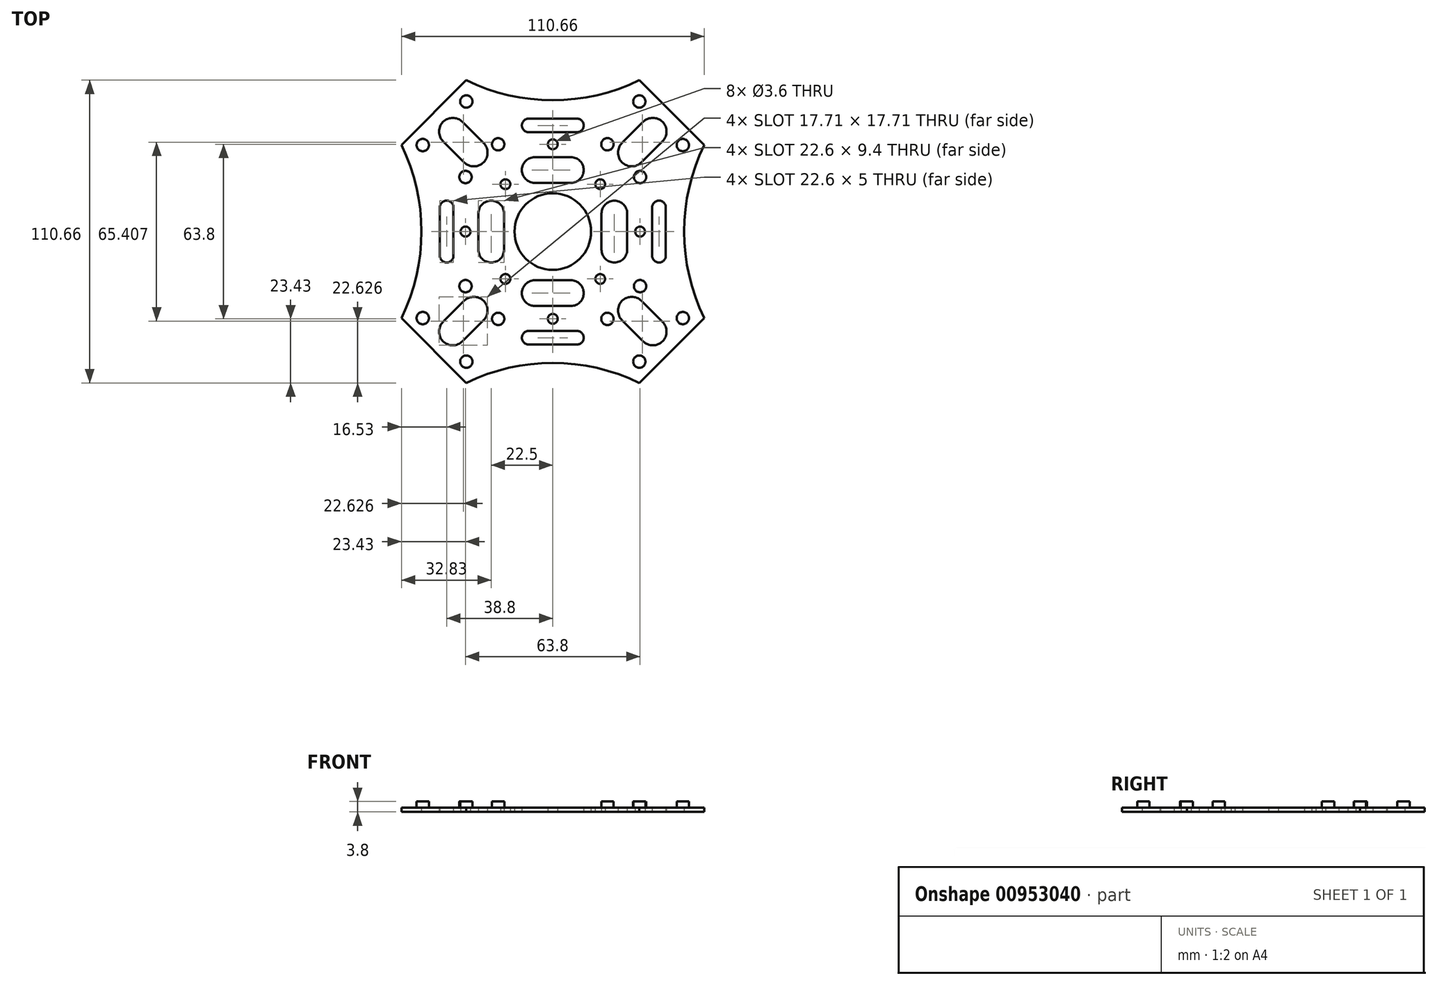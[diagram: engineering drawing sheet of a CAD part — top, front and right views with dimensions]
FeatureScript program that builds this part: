
annotation { "Feature Type Name" : "Feature", "Feature Type Description" : "" }
export const myFeature = defineFeature(function(context is Context, id is Id, definition is map)
    precondition{}
    {
        {
            var Q0;
            Q0=qCreatedBy(makeId("Top.planeOp"),FACE);
            var sketch = newSketch(context, id + "F0", { "sketchPlane" : qUnion([Q0])});
            skCircle(sketch, "E0", {"center": v(0, 0) * mm, "radius": 14 * mm});
            skLineSegment(sketch, "E1", {"start": v(0, 0) * mm, "end": v(83.05, 0) * mm, "construction": true});
            skLineSegment(sketch, "E2", {"start": v(0, 0) * mm, "end": v(67.55, 67.55) * mm, "construction": true});
            skLineSegment(sketch, "E3", {"start": v(17.8, 0) * mm, "end": v(17.8, 6.6) * mm});
            skLineSegment(sketch, "E4", {"start": v(27.2, 0) * mm, "end": v(27.2, 6.6) * mm});
            skArc(sketch, "E5", {"start": v(27.2, 6.6) * mm, "mid": v(22.5, 11.3) * mm, "end": v(17.8, 6.6) * mm});
            skLineSegment(sketch, "E6", {"start": v(36.3, 0) * mm, "end": v(36.3, 8.8) * mm});
            skLineSegment(sketch, "E7", {"start": v(41.3, 0) * mm, "end": v(41.3, 8.8) * mm});
            skArc(sketch, "E8", {"start": v(41.3, 8.8) * mm, "mid": v(38.8, 11.3) * mm, "end": v(36.3, 8.8) * mm});
            skArc(sketch, "E9", {"start": v(33.7, 0) * mm, "mid": v(31.9, 1.8) * mm, "end": v(30.1, 0) * mm});
            skLineSegment(sketch, "E10", {"start": v(32.39, 25.31) * mm, "end": v(40.1, 33.02) * mm});
            skArc(sketch, "E11", {"start": v(32.39, 25.31) * mm, "mid": v(28.85, 23.85) * mm, "end": v(25.31, 25.31) * mm});
            skArc(sketch, "E12", {"start": v(40.1, 33.02) * mm, "mid": v(41.56, 36.56) * mm, "end": v(40.1, 40.1) * mm});
            skLineSegment(sketch, "E13", {"start": v(43.49, 43.49) * mm, "end": v(55.33, 31.64) * mm});
            skArc(sketch, "E14", {"start": v(55.33, 31.64) * mm, "mid": v(49.86, 16.24) * mm, "end": v(48, 0) * mm});
            skArc(sketch, "E15", {"start": v(16.05, 16.05) * mm, "mid": v(18.6, 16.05) * mm, "end": v(18.6, 18.6) * mm});
            skLineSegment(sketch, "E16.MirrorCS", {"start": v(43.49, 43.49) * mm, "end": v(31.64, 55.33) * mm});
            skArc(sketch, "E17.MirrorCS", {"start": v(31.64, 55.33) * mm, "mid": v(16.24, 49.86) * mm, "end": v(0, 48) * mm});
            skArc(sketch, "E18.MirrorCS", {"start": v(33.02, 40.1) * mm, "mid": v(36.56, 41.56) * mm, "end": v(40.1, 40.1) * mm});
            skLineSegment(sketch, "E19.MirrorCS", {"start": v(25.31, 32.39) * mm, "end": v(33.02, 40.1) * mm});
            skArc(sketch, "E20.MirrorCS", {"start": v(25.31, 32.39) * mm, "mid": v(23.85, 28.85) * mm, "end": v(25.31, 25.31) * mm});
            skArc(sketch, "E21.MirrorCS", {"start": v(6.6, 27.2) * mm, "mid": v(11.3, 22.5) * mm, "end": v(6.6, 17.8) * mm});
            skLineSegment(sketch, "E22.MirrorCS", {"start": v(0, 17.8) * mm, "end": v(6.6, 17.8) * mm});
            skLineSegment(sketch, "E23.MirrorCS", {"start": v(0, 27.2) * mm, "end": v(6.6, 27.2) * mm});
            skLineSegment(sketch, "E24.MirrorCS", {"start": v(0, 36.3) * mm, "end": v(8.8, 36.3) * mm});
            skArc(sketch, "E25.MirrorCS", {"start": v(8.8, 41.3) * mm, "mid": v(11.3, 38.8) * mm, "end": v(8.8, 36.3) * mm});
            skLineSegment(sketch, "E26.MirrorCS", {"start": v(0, 41.3) * mm, "end": v(8.8, 41.3) * mm});
            skArc(sketch, "E27.MirrorCS", {"start": v(55.33, -31.64) * mm, "mid": v(49.86, -16.24) * mm, "end": v(48, 0) * mm});
            skLineSegment(sketch, "E28.MirrorCS", {"start": v(41.3, 0) * mm, "end": v(41.3, -8.8) * mm});
            skLineSegment(sketch, "E29.MirrorCS", {"start": v(36.3, 0) * mm, "end": v(36.3, -8.8) * mm});
            skLineSegment(sketch, "E30.MirrorCS", {"start": v(27.2, 0) * mm, "end": v(27.2, -6.6) * mm});
            skLineSegment(sketch, "E31.MirrorCS", {"start": v(17.8, 0) * mm, "end": v(17.8, -6.6) * mm});
            skArc(sketch, "E32.MirrorCS", {"start": v(27.2, -6.6) * mm, "mid": v(22.5, -11.3) * mm, "end": v(17.8, -6.6) * mm});
            skArc(sketch, "E33.MirrorCS", {"start": v(41.3, -8.8) * mm, "mid": v(38.8, -11.3) * mm, "end": v(36.3, -8.8) * mm});
            skLineSegment(sketch, "E34.MirrorCS", {"start": v(32.39, -25.31) * mm, "end": v(40.1, -33.02) * mm});
            skArc(sketch, "E35.MirrorCS", {"start": v(32.39, -25.31) * mm, "mid": v(28.85, -23.85) * mm, "end": v(25.31, -25.31) * mm});
            skArc(sketch, "E36.MirrorCS", {"start": v(25.31, -32.39) * mm, "mid": v(23.85, -28.85) * mm, "end": v(25.31, -25.31) * mm});
            skLineSegment(sketch, "E37.MirrorCS", {"start": v(25.31, -32.39) * mm, "end": v(33.02, -40.1) * mm});
            skArc(sketch, "E38.MirrorCS", {"start": v(33.02, -40.1) * mm, "mid": v(36.56, -41.56) * mm, "end": v(40.1, -40.1) * mm});
            skArc(sketch, "E39.MirrorCS", {"start": v(40.1, -33.02) * mm, "mid": v(41.56, -36.56) * mm, "end": v(40.1, -40.1) * mm});
            skLineSegment(sketch, "E40.MirrorCS", {"start": v(43.49, -43.49) * mm, "end": v(55.33, -31.64) * mm});
            skLineSegment(sketch, "E41.MirrorCS", {"start": v(43.49, -43.49) * mm, "end": v(31.64, -55.33) * mm});
            skArc(sketch, "E42.MirrorCS", {"start": v(31.64, -55.33) * mm, "mid": v(16.24, -49.86) * mm, "end": v(0, -48) * mm});
            skLineSegment(sketch, "E43.MirrorCS", {"start": v(0, -41.3) * mm, "end": v(8.8, -41.3) * mm});
            skArc(sketch, "E44.MirrorCS", {"start": v(8.8, -41.3) * mm, "mid": v(11.3, -38.8) * mm, "end": v(8.8, -36.3) * mm});
            skLineSegment(sketch, "E45.MirrorCS", {"start": v(0, -36.3) * mm, "end": v(8.8, -36.3) * mm});
            skLineSegment(sketch, "E46.MirrorCS", {"start": v(0, -27.2) * mm, "end": v(6.6, -27.2) * mm});
            skArc(sketch, "E47.MirrorCS", {"start": v(6.6, -27.2) * mm, "mid": v(11.3, -22.5) * mm, "end": v(6.6, -17.8) * mm});
            skLineSegment(sketch, "E48.MirrorCS", {"start": v(0, -17.8) * mm, "end": v(6.6, -17.8) * mm});
            skArc(sketch, "E49.MirrorCS", {"start": v(16.05, 16.05) * mm, "mid": v(16.05, 18.6) * mm, "end": v(18.6, 18.6) * mm});
            skArc(sketch, "E50.MirrorCS", {"start": v(33.7, 0) * mm, "mid": v(31.9, -1.8) * mm, "end": v(30.1, 0) * mm});
            skArc(sketch, "E51.MirrorCS", {"start": v(16.05, -16.05) * mm, "mid": v(18.6, -16.05) * mm, "end": v(18.6, -18.6) * mm});
            skArc(sketch, "E52.MirrorCS", {"start": v(16.05, -16.05) * mm, "mid": v(16.05, -18.6) * mm, "end": v(18.6, -18.6) * mm});
            skArc(sketch, "E53.MirrorCS", {"start": v(0, 33.7) * mm, "mid": v(1.8, 31.9) * mm, "end": v(0, 30.1) * mm});
            skArc(sketch, "E54.MirrorCS", {"start": v(0, -33.7) * mm, "mid": v(1.8, -31.9) * mm, "end": v(0, -30.1) * mm});
            skArc(sketch, "E55.MirrorCS", {"start": v(-33.7, 0) * mm, "mid": v(-31.9, -1.8) * mm, "end": v(-30.1, 0) * mm});
            skArc(sketch, "E56.MirrorCS", {"start": v(-33.7, 0) * mm, "mid": v(-31.9, 1.8) * mm, "end": v(-30.1, 0) * mm});
            skArc(sketch, "E57.MirrorCS", {"start": v(-16.05, 16.05) * mm, "mid": v(-18.6, 16.05) * mm, "end": v(-18.6, 18.6) * mm});
            skArc(sketch, "E58.MirrorCS", {"start": v(-16.05, -16.05) * mm, "mid": v(-18.6, -16.05) * mm, "end": v(-18.6, -18.6) * mm});
            skArc(sketch, "E59.MirrorCS", {"start": v(0, -33.7) * mm, "mid": v(-1.8, -31.9) * mm, "end": v(0, -30.1) * mm});
            skArc(sketch, "E60.MirrorCS", {"start": v(-16.05, 16.05) * mm, "mid": v(-16.05, 18.6) * mm, "end": v(-18.6, 18.6) * mm});
            skArc(sketch, "E61.MirrorCS", {"start": v(-16.05, -16.05) * mm, "mid": v(-16.05, -18.6) * mm, "end": v(-18.6, -18.6) * mm});
            skLineSegment(sketch, "E62.MirrorCS", {"start": v(0, 41.3) * mm, "end": v(-8.8, 41.3) * mm});
            skLineSegment(sketch, "E63.MirrorCS", {"start": v(-36.3, 0) * mm, "end": v(-36.3, -8.8) * mm});
            skArc(sketch, "E64.MirrorCS", {"start": v(-41.3, -8.8) * mm, "mid": v(-38.8, -11.3) * mm, "end": v(-36.3, -8.8) * mm});
            skArc(sketch, "E65.MirrorCS", {"start": v(-27.2, -6.6) * mm, "mid": v(-22.5, -11.3) * mm, "end": v(-17.8, -6.6) * mm});
            skLineSegment(sketch, "E66.MirrorCS", {"start": v(0, -27.2) * mm, "end": v(-6.6, -27.2) * mm});
            skLineSegment(sketch, "E67.MirrorCS", {"start": v(-36.3, 0) * mm, "end": v(-36.3, 8.8) * mm});
            skLineSegment(sketch, "E68.MirrorCS", {"start": v(-25.31, 32.39) * mm, "end": v(-33.02, 40.1) * mm});
            skLineSegment(sketch, "E69.MirrorCS", {"start": v(0, 36.3) * mm, "end": v(-8.8, 36.3) * mm});
            skLineSegment(sketch, "E70.MirrorCS", {"start": v(0, 17.8) * mm, "end": v(-6.6, 17.8) * mm});
            skLineSegment(sketch, "E71.MirrorCS", {"start": v(-27.2, 0) * mm, "end": v(-27.2, 6.6) * mm});
            skArc(sketch, "E72.MirrorCS", {"start": v(-8.8, 41.3) * mm, "mid": v(-11.3, 38.8) * mm, "end": v(-8.8, 36.3) * mm});
            skArc(sketch, "E73.MirrorCS", {"start": v(0, 33.7) * mm, "mid": v(-1.8, 31.9) * mm, "end": v(0, 30.1) * mm});
            skLineSegment(sketch, "E74.MirrorCS", {"start": v(-27.2, 0) * mm, "end": v(-27.2, -6.6) * mm});
            skArc(sketch, "E75.MirrorCS", {"start": v(-6.6, 27.2) * mm, "mid": v(-11.3, 22.5) * mm, "end": v(-6.6, 17.8) * mm});
            skLineSegment(sketch, "E76.MirrorCS", {"start": v(0, -36.3) * mm, "end": v(-8.8, -36.3) * mm});
            skArc(sketch, "E77.MirrorCS", {"start": v(-27.2, 6.6) * mm, "mid": v(-22.5, 11.3) * mm, "end": v(-17.8, 6.6) * mm});
            skArc(sketch, "E78.MirrorCS", {"start": v(-25.31, 32.39) * mm, "mid": v(-23.85, 28.85) * mm, "end": v(-25.31, 25.31) * mm});
            skLineSegment(sketch, "E79.MirrorCS", {"start": v(-43.49, -43.49) * mm, "end": v(-31.64, -55.33) * mm});
            skArc(sketch, "E80.MirrorCS", {"start": v(-40.1, -33.02) * mm, "mid": v(-41.56, -36.56) * mm, "end": v(-40.1, -40.1) * mm});
            skLineSegment(sketch, "E81.MirrorCS", {"start": v(-43.49, 43.49) * mm, "end": v(-31.64, 55.33) * mm});
            skLineSegment(sketch, "E82.MirrorCS", {"start": v(-17.8, 0) * mm, "end": v(-17.8, 6.6) * mm});
            skArc(sketch, "E83.MirrorCS", {"start": v(-32.39, 25.31) * mm, "mid": v(-28.85, 23.85) * mm, "end": v(-25.31, 25.31) * mm});
            skArc(sketch, "E84.MirrorCS", {"start": v(-33.02, 40.1) * mm, "mid": v(-36.56, 41.56) * mm, "end": v(-40.1, 40.1) * mm});
            skArc(sketch, "E85.MirrorCS", {"start": v(-33.02, -40.1) * mm, "mid": v(-36.56, -41.56) * mm, "end": v(-40.1, -40.1) * mm});
            skLineSegment(sketch, "E86.MirrorCS", {"start": v(-17.8, 0) * mm, "end": v(-17.8, -6.6) * mm});
            skLineSegment(sketch, "E87.MirrorCS", {"start": v(-41.3, 0) * mm, "end": v(-41.3, 8.8) * mm});
            skArc(sketch, "E88.MirrorCS", {"start": v(-40.1, 33.02) * mm, "mid": v(-41.56, 36.56) * mm, "end": v(-40.1, 40.1) * mm});
            skArc(sketch, "E89.MirrorCS", {"start": v(-31.64, -55.33) * mm, "mid": v(-16.24, -49.86) * mm, "end": v(0, -48) * mm});
            skLineSegment(sketch, "E90.MirrorCS", {"start": v(-41.3, 0) * mm, "end": v(-41.3, -8.8) * mm});
            skArc(sketch, "E91.MirrorCS", {"start": v(-31.64, 55.33) * mm, "mid": v(-16.24, 49.86) * mm, "end": v(0, 48) * mm});
            skArc(sketch, "E92.MirrorCS", {"start": v(-6.6, -27.2) * mm, "mid": v(-11.3, -22.5) * mm, "end": v(-6.6, -17.8) * mm});
            skLineSegment(sketch, "E93.MirrorCS", {"start": v(-43.49, -43.49) * mm, "end": v(-55.33, -31.64) * mm});
            skArc(sketch, "E94.MirrorCS", {"start": v(-55.33, 31.64) * mm, "mid": v(-49.86, 16.24) * mm, "end": v(-48, 0) * mm});
            skArc(sketch, "E95.MirrorCS", {"start": v(-25.31, -32.39) * mm, "mid": v(-23.85, -28.85) * mm, "end": v(-25.31, -25.31) * mm});
            skArc(sketch, "E96.MirrorCS", {"start": v(-55.33, -31.64) * mm, "mid": v(-49.86, -16.24) * mm, "end": v(-48, 0) * mm});
            skArc(sketch, "E97.MirrorCS", {"start": v(-32.39, -25.31) * mm, "mid": v(-28.85, -23.85) * mm, "end": v(-25.31, -25.31) * mm});
            skArc(sketch, "E98.MirrorCS", {"start": v(-8.8, -41.3) * mm, "mid": v(-11.3, -38.8) * mm, "end": v(-8.8, -36.3) * mm});
            skLineSegment(sketch, "E99.MirrorCS", {"start": v(-25.31, -32.39) * mm, "end": v(-33.02, -40.1) * mm});
            skLineSegment(sketch, "E100.MirrorCS", {"start": v(-43.49, 43.49) * mm, "end": v(-55.33, 31.64) * mm});
            skArc(sketch, "E101.MirrorCS", {"start": v(-41.3, 8.8) * mm, "mid": v(-38.8, 11.3) * mm, "end": v(-36.3, 8.8) * mm});
            skLineSegment(sketch, "E102.MirrorCS", {"start": v(0, 27.2) * mm, "end": v(-6.6, 27.2) * mm});
            skLineSegment(sketch, "E103.MirrorCS", {"start": v(0, -41.3) * mm, "end": v(-8.8, -41.3) * mm});
            skLineSegment(sketch, "E104.MirrorCS", {"start": v(-32.39, 25.31) * mm, "end": v(-40.1, 33.02) * mm});
            skLineSegment(sketch, "E105.MirrorCS", {"start": v(0, -17.8) * mm, "end": v(-6.6, -17.8) * mm});
            skLineSegment(sketch, "E106.MirrorCS", {"start": v(-32.39, -25.31) * mm, "end": v(-40.1, -33.02) * mm});
            skSolve(sketch);
        }
        {
            var Q0;
            Q0=makeQuery(id+"F0.imprint","IMPRINT",FACE,{"disambiguationData":[TD([[makeQuery(id+"F0.imprint","IMPRINT",EDGE,{"derivedFrom":sQuery(id+"F0.wireOp",EDGE,"E3")}),1.0]])]});
            extrude(context, id + "F1", {"entities" : qUnion([Q0]), "depth" : 1.6 * mm, "offsetDistance" : 25 * mm});
        }
        {
            var Q0;
            Q0=makeQuery(id+"F1.opExtrude","CAP_FACE",FACE,{"disambiguationData":[OSD([sQuery(id+"F0.wireOp",EDGE,"E3"),sQuery(id+"F0.wireOp",EDGE,"E4"),sQuery(id+"F0.wireOp",EDGE,"E5"),sQuery(id+"F0.wireOp",EDGE,"E6"),sQuery(id+"F0.wireOp",EDGE,"E7"),sQuery(id+"F0.wireOp",EDGE,"E8"),sQuery(id+"F0.wireOp",EDGE,"E9"),sQuery(id+"F0.wireOp",EDGE,"E10"),sQuery(id+"F0.wireOp",EDGE,"E11"),sQuery(id+"F0.wireOp",EDGE,"E12"),sQuery(id+"F0.wireOp",EDGE,"E13"),sQuery(id+"F0.wireOp",EDGE,"E14"),sQuery(id+"F0.wireOp",EDGE,"E15"),sQuery(id+"F0.wireOp",EDGE,"E16.MirrorCS"),sQuery(id+"F0.wireOp",EDGE,"E17.MirrorCS"),sQuery(id+"F0.wireOp",EDGE,"E18.MirrorCS"),sQuery(id+"F0.wireOp",EDGE,"E19.MirrorCS"),sQuery(id+"F0.wireOp",EDGE,"E20.MirrorCS"),sQuery(id+"F0.wireOp",EDGE,"E21.MirrorCS"),sQuery(id+"F0.wireOp",EDGE,"E22.MirrorCS"),sQuery(id+"F0.wireOp",EDGE,"E23.MirrorCS"),sQuery(id+"F0.wireOp",EDGE,"E24.MirrorCS"),sQuery(id+"F0.wireOp",EDGE,"E25.MirrorCS"),sQuery(id+"F0.wireOp",EDGE,"E26.MirrorCS"),sQuery(id+"F0.wireOp",EDGE,"E27.MirrorCS"),sQuery(id+"F0.wireOp",EDGE,"E28.MirrorCS"),sQuery(id+"F0.wireOp",EDGE,"E29.MirrorCS"),sQuery(id+"F0.wireOp",EDGE,"E30.MirrorCS"),sQuery(id+"F0.wireOp",EDGE,"E31.MirrorCS"),sQuery(id+"F0.wireOp",EDGE,"E32.MirrorCS"),sQuery(id+"F0.wireOp",EDGE,"E33.MirrorCS"),sQuery(id+"F0.wireOp",EDGE,"E34.MirrorCS"),sQuery(id+"F0.wireOp",EDGE,"E35.MirrorCS"),sQuery(id+"F0.wireOp",EDGE,"E36.MirrorCS"),sQuery(id+"F0.wireOp",EDGE,"E37.MirrorCS"),sQuery(id+"F0.wireOp",EDGE,"E38.MirrorCS"),sQuery(id+"F0.wireOp",EDGE,"E39.MirrorCS"),sQuery(id+"F0.wireOp",EDGE,"E40.MirrorCS"),sQuery(id+"F0.wireOp",EDGE,"E41.MirrorCS"),sQuery(id+"F0.wireOp",EDGE,"E42.MirrorCS"),sQuery(id+"F0.wireOp",EDGE,"E43.MirrorCS"),sQuery(id+"F0.wireOp",EDGE,"E44.MirrorCS"),sQuery(id+"F0.wireOp",EDGE,"E45.MirrorCS"),sQuery(id+"F0.wireOp",EDGE,"E46.MirrorCS"),sQuery(id+"F0.wireOp",EDGE,"E47.MirrorCS"),sQuery(id+"F0.wireOp",EDGE,"E48.MirrorCS"),sQuery(id+"F0.wireOp",EDGE,"E49.MirrorCS"),sQuery(id+"F0.wireOp",EDGE,"E50.MirrorCS"),sQuery(id+"F0.wireOp",EDGE,"E51.MirrorCS"),sQuery(id+"F0.wireOp",EDGE,"E52.MirrorCS"),sQuery(id+"F0.wireOp",EDGE,"E53.MirrorCS"),sQuery(id+"F0.wireOp",EDGE,"E54.MirrorCS"),sQuery(id+"F0.wireOp",EDGE,"E55.MirrorCS"),sQuery(id+"F0.wireOp",EDGE,"E56.MirrorCS"),sQuery(id+"F0.wireOp",EDGE,"E57.MirrorCS"),sQuery(id+"F0.wireOp",EDGE,"E58.MirrorCS"),sQuery(id+"F0.wireOp",EDGE,"E59.MirrorCS"),sQuery(id+"F0.wireOp",EDGE,"E60.MirrorCS"),sQuery(id+"F0.wireOp",EDGE,"E61.MirrorCS"),sQuery(id+"F0.wireOp",EDGE,"E62.MirrorCS"),sQuery(id+"F0.wireOp",EDGE,"E63.MirrorCS"),sQuery(id+"F0.wireOp",EDGE,"E64.MirrorCS"),sQuery(id+"F0.wireOp",EDGE,"E65.MirrorCS"),sQuery(id+"F0.wireOp",EDGE,"E66.MirrorCS"),sQuery(id+"F0.wireOp",EDGE,"E67.MirrorCS"),sQuery(id+"F0.wireOp",EDGE,"E68.MirrorCS"),sQuery(id+"F0.wireOp",EDGE,"E69.MirrorCS"),sQuery(id+"F0.wireOp",EDGE,"E70.MirrorCS"),sQuery(id+"F0.wireOp",EDGE,"E71.MirrorCS"),sQuery(id+"F0.wireOp",EDGE,"E72.MirrorCS"),sQuery(id+"F0.wireOp",EDGE,"E73.MirrorCS"),sQuery(id+"F0.wireOp",EDGE,"E74.MirrorCS"),sQuery(id+"F0.wireOp",EDGE,"E75.MirrorCS"),sQuery(id+"F0.wireOp",EDGE,"E76.MirrorCS"),sQuery(id+"F0.wireOp",EDGE,"E77.MirrorCS"),sQuery(id+"F0.wireOp",EDGE,"E78.MirrorCS"),sQuery(id+"F0.wireOp",EDGE,"E79.MirrorCS"),sQuery(id+"F0.wireOp",EDGE,"E80.MirrorCS"),sQuery(id+"F0.wireOp",EDGE,"E81.MirrorCS"),sQuery(id+"F0.wireOp",EDGE,"E82.MirrorCS"),sQuery(id+"F0.wireOp",EDGE,"E83.MirrorCS"),sQuery(id+"F0.wireOp",EDGE,"E84.MirrorCS"),sQuery(id+"F0.wireOp",EDGE,"E85.MirrorCS"),sQuery(id+"F0.wireOp",EDGE,"E86.MirrorCS"),sQuery(id+"F0.wireOp",EDGE,"E87.MirrorCS"),sQuery(id+"F0.wireOp",EDGE,"E88.MirrorCS"),sQuery(id+"F0.wireOp",EDGE,"E89.MirrorCS"),sQuery(id+"F0.wireOp",EDGE,"E90.MirrorCS"),sQuery(id+"F0.wireOp",EDGE,"E91.MirrorCS"),sQuery(id+"F0.wireOp",EDGE,"E92.MirrorCS"),sQuery(id+"F0.wireOp",EDGE,"E93.MirrorCS"),sQuery(id+"F0.wireOp",EDGE,"E94.MirrorCS"),sQuery(id+"F0.wireOp",EDGE,"E95.MirrorCS"),sQuery(id+"F0.wireOp",EDGE,"E96.MirrorCS"),sQuery(id+"F0.wireOp",EDGE,"E97.MirrorCS"),sQuery(id+"F0.wireOp",EDGE,"E98.MirrorCS"),sQuery(id+"F0.wireOp",EDGE,"E99.MirrorCS"),sQuery(id+"F0.wireOp",EDGE,"E100.MirrorCS"),sQuery(id+"F0.wireOp",EDGE,"E101.MirrorCS"),sQuery(id+"F0.wireOp",EDGE,"E102.MirrorCS"),sQuery(id+"F0.wireOp",EDGE,"E103.MirrorCS"),sQuery(id+"F0.wireOp",EDGE,"E104.MirrorCS"),sQuery(id+"F0.wireOp",EDGE,"E105.MirrorCS"),sQuery(id+"F0.wireOp",EDGE,"E106.MirrorCS"),sQuery(id+"F0.wireOp",EDGE,"E0")])],"isStart":false});
            var sketch = newSketch(context, id + "F2", { "sketchPlane" : qUnion([Q0])});
            skCircle(sketch, "E107", {"center": v(31.9, 19.95) * mm, "radius": 2.25 * mm});
            skCircle(sketch, "E108", {"center": v(47.53, 31.62) * mm, "radius": 2.25 * mm});
            skCircle(sketch, "E109.MirrorC", {"center": v(31.62, 47.53) * mm, "radius": 2.25 * mm});
            skCircle(sketch, "E110.MirrorC", {"center": v(19.95, 31.9) * mm, "radius": 2.25 * mm});
            skCircle(sketch, "E111.MirrorC", {"center": v(47.53, -31.62) * mm, "radius": 2.25 * mm});
            skCircle(sketch, "E112.MirrorC", {"center": v(31.9, -19.95) * mm, "radius": 2.25 * mm});
            skCircle(sketch, "E113.MirrorC", {"center": v(19.95, -31.9) * mm, "radius": 2.25 * mm});
            skCircle(sketch, "E114.MirrorC", {"center": v(31.62, -47.53) * mm, "radius": 2.25 * mm});
            skCircle(sketch, "E115.MirrorC", {"center": v(-31.9, -19.95) * mm, "radius": 2.25 * mm});
            skCircle(sketch, "E116.MirrorC", {"center": v(-31.9, 19.95) * mm, "radius": 2.25 * mm});
            skCircle(sketch, "E117.MirrorC", {"center": v(-47.53, -31.62) * mm, "radius": 2.25 * mm});
            skCircle(sketch, "E118.MirrorC", {"center": v(-31.62, 47.53) * mm, "radius": 2.25 * mm});
            skCircle(sketch, "E119.MirrorC", {"center": v(-47.53, 31.62) * mm, "radius": 2.25 * mm});
            skCircle(sketch, "E120.MirrorC", {"center": v(-31.62, -47.53) * mm, "radius": 2.25 * mm});
            skCircle(sketch, "E121.MirrorC", {"center": v(-19.95, 31.9) * mm, "radius": 2.25 * mm});
            skCircle(sketch, "E122.MirrorC", {"center": v(-19.95, -31.9) * mm, "radius": 2.25 * mm});
            skSolve(sketch);
        }
        {
            var Q0;
            Q0 = qSketchRegion(id + "F2", true);
            extrude(context, id + "F3", {"entities" : qUnion([Q0]), "operationType" : NewBodyOperationType.ADD, "depth" : 2.2 * mm, "offsetDistance" : 25 * mm});
        }
    });
